# Revit family: 63_UN_Lightline_WDO L1200_Norton
name_source: partatom
category: Lighting Fixtures
units: mm (PartAtom-declared; Revit-internal decimal feet)

## family parameters
Always vertical = Yes
Cut with Voids When Loaded = No
Light Source = Yes
OmniClass Number = 23.80.70.11.14.11
OmniClass Title = Downlights
Part Type = Normal
Room Calculation Point = Yes
Round Connector Dimension = Use Diameter
Shared = No
Work Plane-Based = No

## types (2) — shared parameters
Assembly Code = 63.0
Bracket_Distance = 800 mm  [stored 2.62467 ft]
Color Filter = 16777215
Dimming Lamp Color Temperature Shift = <None>
Emit Shape Visible in Rendering = No
Emit from Rectangle Length = 101 mm  [stored 0.331365 ft]
Emit from Rectangle Width = 1240 mm  [stored 4.06824 ft]
Housing_Material = Laminate, White
IK Value = IK08
IP Value = IP66
IfcExportAs = IfcLightFixtureType
IfcExportType = USERDEFINED
Lamp = LED
Length = 1280 mm  [stored 4.19948 ft]
Manufacturer = Norton
Model = WDO
Tilt Angle = 60.00°
Type Comments = L1200
URL = https://www.ivlibrary.com
Voltage = 230 V
calc_length = 1240 mm  [stored 4.06824 ft]

## per-type parameters (varying)
| type | Apparent Load | Luminous Flux (lm) | Photometric Web File | Wattage Comments |
| WDO 84 1 2400 1250 | 15 VA | 2400 lm | WDO84124001250_LDT.ies | 15W |
| WDO 84 1 4200 1250 | 31 VA | 4200 lm | WDO84142001250_LDT.ies | 31W |

note: [stored X ft] marks values corroborated as IEEE doubles in the binary element streams (Revit-internal decimal feet)

## geometry (parser evidence)
native form markers: Sweep x5
no freeform markers — native parametric forms only
